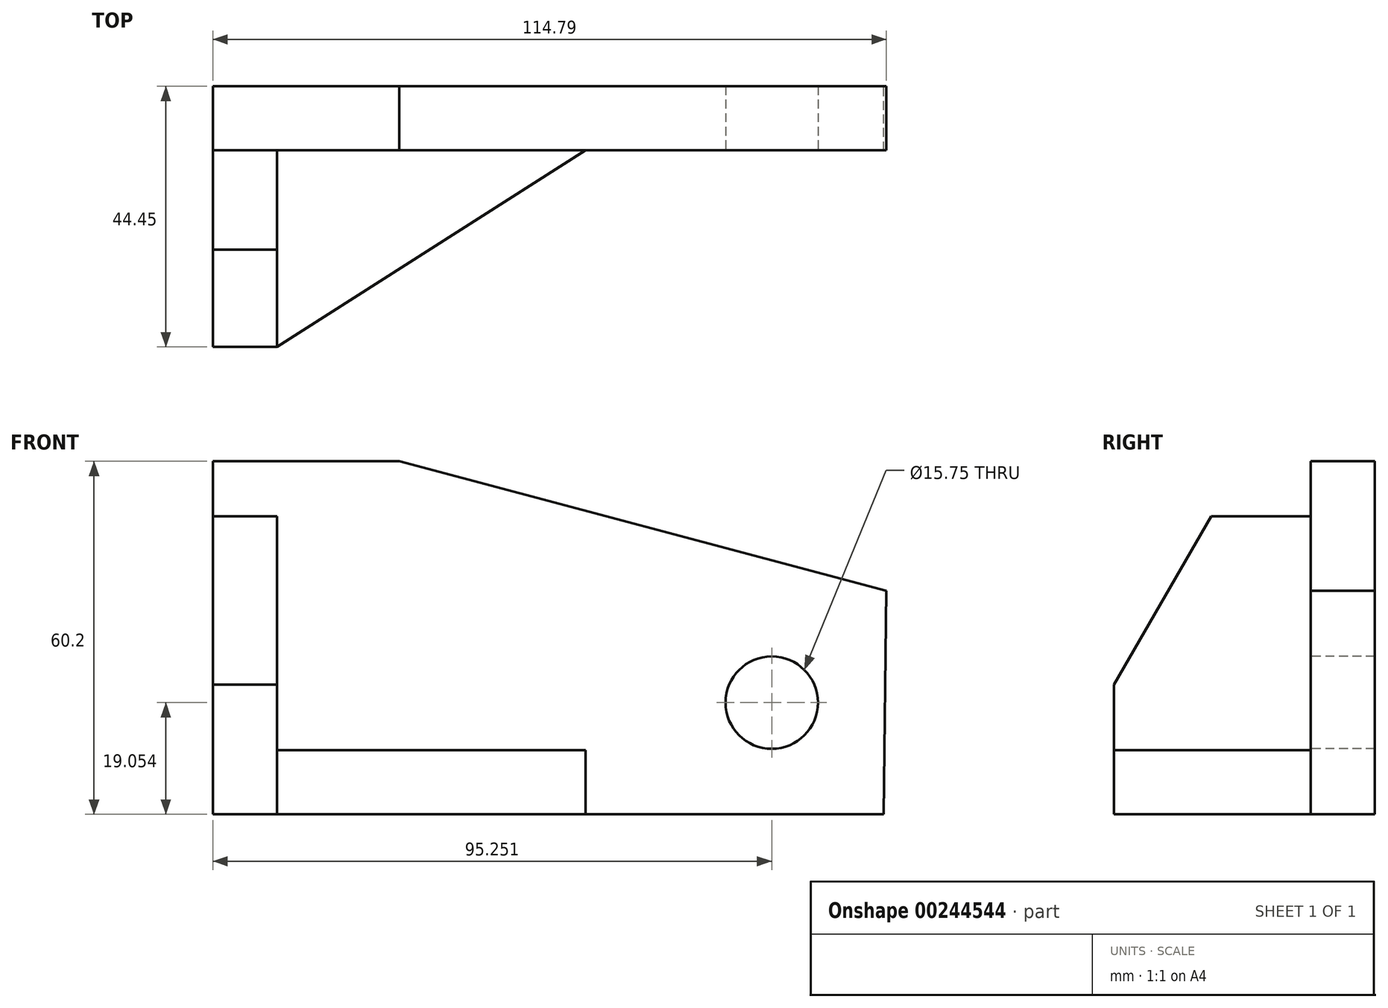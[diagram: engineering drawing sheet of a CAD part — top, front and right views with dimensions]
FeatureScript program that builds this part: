
annotation { "Feature Type Name" : "Feature", "Feature Type Description" : "" }
export const myFeature = defineFeature(function(context is Context, id is Id, definition is map)
    precondition{}
    {
        {
            var Q0;
            Q0=qCreatedBy(makeId("Front.planeOp"),FACE);
            var sketch = newSketch(context, id + "F0", { "sketchPlane" : qUnion([Q0])});
            skLineSegment(sketch, "E0.bottom", {"start": v(-94.92, 37.9) * mm, "end": v(-63.17, 37.9) * mm});
            skLineSegment(sketch, "E0.top", {"start": v(-94.92, -22.3) * mm, "end": v(-63.17, -22.3) * mm});
            skLineSegment(sketch, "E0.left", {"start": v(-94.92, 37.9) * mm, "end": v(-94.92, -22.3) * mm});
            skLineSegment(sketch, "E1", {"start": v(-63.17, -22.3) * mm, "end": v(19.38, -22.3) * mm});
            skPoint(sketch, "E2", {"position": v(0.33, -3.25) * mm});
            skLineSegment(sketch, "E3", {"start": v(19.38, -22.3) * mm, "end": v(19.87, 15.8) * mm});
            skLineSegment(sketch, "E4", {"start": v(-63.17, 37.9) * mm, "end": v(19.87, 15.8) * mm});
            skSolve(sketch);
        }
        {
            var Q0;
            Q0=makeQuery(id+"F0.imprint","IMPRINT",FACE,{"disambiguationData":[TD([[makeQuery(id+"F0.imprint","IMPRINT",EDGE,{"derivedFrom":sQuery(id+"F0.wireOp",EDGE,"E0.bottom")}),-1.0]])]});
            extrude(context, id + "F1", {"entities" : qUnion([Q0]), "depth" : 10.92 * mm});
        }
        {
            var Q0;
            Q0=makeQuery(id+"F1.opExtrude","CAP_FACE",FACE,{"disambiguationData":[OSD([sQuery(id+"F0.wireOp",EDGE,"E0.bottom"),sQuery(id+"F0.wireOp",EDGE,"E0.top"),sQuery(id+"F0.wireOp",EDGE,"E0.left"),sQuery(id+"F0.wireOp",EDGE,"E1"),sQuery(id+"F0.wireOp",EDGE,"PZj4ohab-rFBr-Dsya-SFYZ-FZSW6xQUwl1A"),sQuery(id+"F0.wireOp",EDGE,"DjLbbVJZ-fkTx-wbr6-xFs6-VdaemuGiisQY")])],"isStart":false});
            var sketch = newSketch(context, id + "F2", { "sketchPlane" : qUnion([Q0])});
            skPoint(sketch, "E5", {"position": v(0.33, -3.25) * mm});
            skPoint(sketch, "E6.end.orphan", {"position": v(19.38, -3.5) * mm});
            skSolve(sketch);
        }
        {
            var Q0;
            Q0=sQuery(id+"F2.wireOp",VERTEX,"E5");
            var Q1;
            Q1=makeQuery(id+"F1.opExtrude","SWEPT_BODY",BODY,{"disambiguationData":[OSD([sQuery(id+"F0.wireOp",EDGE,"E0.bottom"),sQuery(id+"F0.wireOp",EDGE,"E0.top"),sQuery(id+"F0.wireOp",EDGE,"E0.left"),sQuery(id+"F0.wireOp",EDGE,"E1"),sQuery(id+"F0.wireOp",EDGE,"E3"),sQuery(id+"F0.wireOp",EDGE,"E4")])]});
            hole(context, id + "F3", {"style" : HoleStyle.SIMPLE, "endStyle" : HoleEndStyle.THROUGH, "holeDiameter" : 15.75 * mm, "tappedDepth" : 12.7 * mm, "tapClearance" : 3, "locations" : qUnion([Q0]), "scope" : qUnion([Q1])});
        }
        {
            var Q0;
            Q0=makeQuery(id+"F1.opExtrude","CAP_FACE",FACE,{"disambiguationData":[OSD([sQuery(id+"F0.wireOp",EDGE,"E0.bottom"),sQuery(id+"F0.wireOp",EDGE,"E0.top"),sQuery(id+"F0.wireOp",EDGE,"E0.left"),sQuery(id+"F0.wireOp",EDGE,"E1"),sQuery(id+"F0.wireOp",EDGE,"E3"),sQuery(id+"F0.wireOp",EDGE,"E4")])],"isStart":false});
            var sketch = newSketch(context, id + "F4", { "sketchPlane" : qUnion([Q0])});
            skLineSegment(sketch, "E7.bottom", {"start": v(-94.92, -22.3) * mm, "end": v(-84, -22.3) * mm});
            skLineSegment(sketch, "E7.top", {"start": v(-94.92, 28.5) * mm, "end": v(-84, 28.5) * mm});
            skLineSegment(sketch, "E7.left", {"start": v(-94.92, -22.3) * mm, "end": v(-94.92, 28.5) * mm});
            skLineSegment(sketch, "E7.right", {"start": v(-84, -22.3) * mm, "end": v(-84, 28.5) * mm});
            skLineSegment(sketch, "E8.bottom", {"start": v(-94.92, -22.3) * mm, "end": v(-31.42, -22.3) * mm});
            skLineSegment(sketch, "E8.top", {"start": v(-84, -11.37) * mm, "end": v(-31.42, -11.37) * mm});
            skLineSegment(sketch, "E8.left", {"start": v(-94.92, -22.3) * mm, "end": v(-94.92, -11.37) * mm});
            skLineSegment(sketch, "E8.right", {"start": v(-31.42, -22.3) * mm, "end": v(-31.42, -11.37) * mm});
            skSolve(sketch);
        }
        {
            var Q0;
            {var subQ3=sQuery(id+"F4.wireOp",EDGE,"E8.top");Q0=makeQuery(id+"F4.imprint","IMPRINT",FACE,{"disambiguationData":[TD([[makeQuery(id+"F4.imprint","IMPRINT",EDGE,{"derivedFrom":subQ3}),-1.0]])]});}
            var Q1;
            {var subQ1=sQuery(id+"F4.wireOp",EDGE,"E7.top");Q1=makeQuery(id+"F4.imprint","IMPRINT",FACE,{"disambiguationData":[TD([[makeQuery(id+"F4.imprint","IMPRINT",EDGE,{"derivedFrom":subQ1}),-1.0]])]});}
            extrude(context, id + "F5", {"entities" : qUnion([Q0, Q1]), "operationType" : NewBodyOperationType.ADD, "depth" : 33.53 * mm});
        }
        {
            var Q0;
            Q0=makeQuery(id+"F5.opExtrude","SWEPT_FACE",FACE,{"disambiguationData":[OSD([sQuery(id+"F4.wireOp",EDGE,"E7.right")])]});
            var sketch = newSketch(context, id + "F6", { "sketchPlane" : qUnion([Q0])});
            skLineSegment(sketch, "E9", {"start": v(-27.88, 28.5) * mm, "end": v(-44.45, -0.2) * mm});
            skLineSegment(sketch, "E10", {"start": v(-44.45, -0.2) * mm, "end": v(-44.45, 28.5) * mm});
            skLineSegment(sketch, "E11", {"start": v(-44.45, -11.37) * mm, "end": v(-44.45, -0.2) * mm});
            skLineSegment(sketch, "E12", {"start": v(-44.45, 28.5) * mm, "end": v(-27.88, 28.5) * mm});
            skSolve(sketch);
        }
        {
            var Q0;
            Q0=makeQuery(id+"F6.imprint","IMPRINT",FACE,{"disambiguationData":[TD([[makeQuery(id+"F6.imprint","IMPRINT",EDGE,{"derivedFrom":sQuery(id+"F6.wireOp",EDGE,"E9")}),-1.0]])]});
            extrude(context, id + "F7", {"entities" : qUnion([Q0]), "operationType" : NewBodyOperationType.REMOVE, "endBound" : BoundingType.THROUGH_ALL, "oppositeDirection" : true, "depth" : 25.4 * mm});
        }
        {
            var Q0;
            Q0=makeQuery(id+"F5.opExtrude","SWEPT_FACE",FACE,{"disambiguationData":[OSD([sQuery(id+"F4.wireOp",EDGE,"E8.top")])]});
            var sketch = newSketch(context, id + "F8", { "sketchPlane" : qUnion([Q0])});
            skLineSegment(sketch, "E13", {"start": v(-84, -44.45) * mm, "end": v(-31.42, -10.92) * mm});
            skSolve(sketch);
        }
        {
            var Q0;
            Q0=makeQuery(id+"F8.imprint","IMPRINT",FACE,{"disambiguationData":[TD([[makeQuery(id+"F8.imprint","IMPRINT",EDGE,{"derivedFrom":sQuery(id+"F8.wireOp",EDGE,"E13")}),-1.0]])]});
            extrude(context, id + "F9", {"entities" : qUnion([Q0]), "operationType" : NewBodyOperationType.REMOVE, "endBound" : BoundingType.THROUGH_ALL, "oppositeDirection" : true, "depth" : 25.4 * mm});
        }
    });
